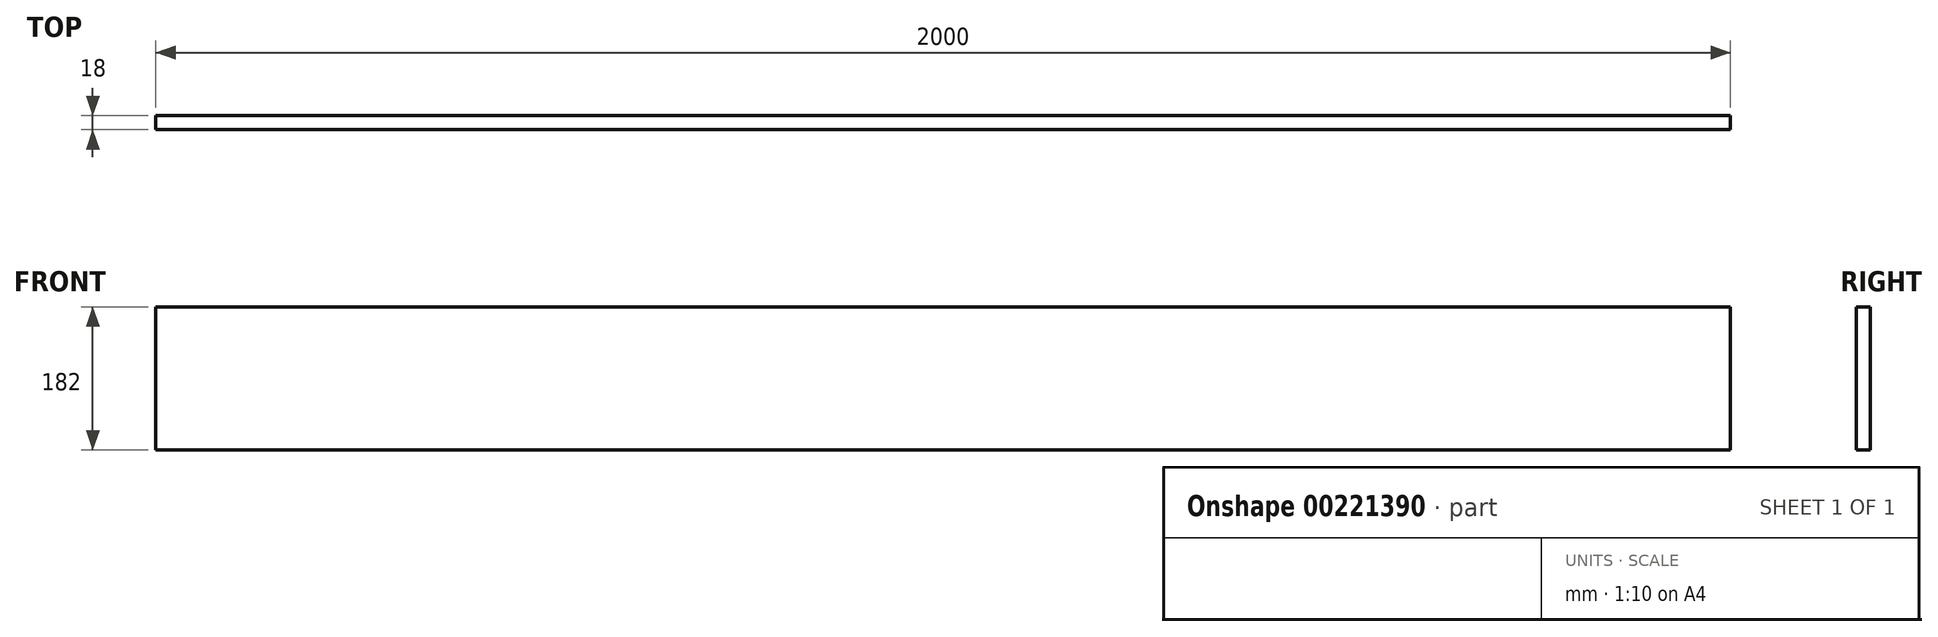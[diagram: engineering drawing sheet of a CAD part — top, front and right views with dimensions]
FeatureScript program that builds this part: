
annotation { "Feature Type Name" : "Feature", "Feature Type Description" : "" }
export const myFeature = defineFeature(function(context is Context, id is Id, definition is map)
    precondition{}
    {
        {
            var Q0;
            Q0=qCreatedBy(makeId("Front.planeOp"),FACE);
            var sketch = newSketch(context, id + "F0", { "sketchPlane" : qUnion([Q0])});
            skLineSegment(sketch, "E0.bottom", {"start": v(1000, -91) * mm, "end": v(-1000, -91) * mm});
            skLineSegment(sketch, "E0.top", {"start": v(1000, 91) * mm, "end": v(-1000, 91) * mm});
            skLineSegment(sketch, "E0.left", {"start": v(1000, -91) * mm, "end": v(1000, 91) * mm});
            skLineSegment(sketch, "E0.right", {"start": v(-1000, -91) * mm, "end": v(-1000, 91) * mm});
            skPoint(sketch, "E0.middle", {"position": v(0, 0) * mm});
            skSolve(sketch);
        }
        {
            var Q0;
            Q0 = qSketchRegion(id + "F0", true);
            extrude(context, id + "F1", {"entities" : qUnion([Q0]), "depth" : 18 * mm});
        }
    });
